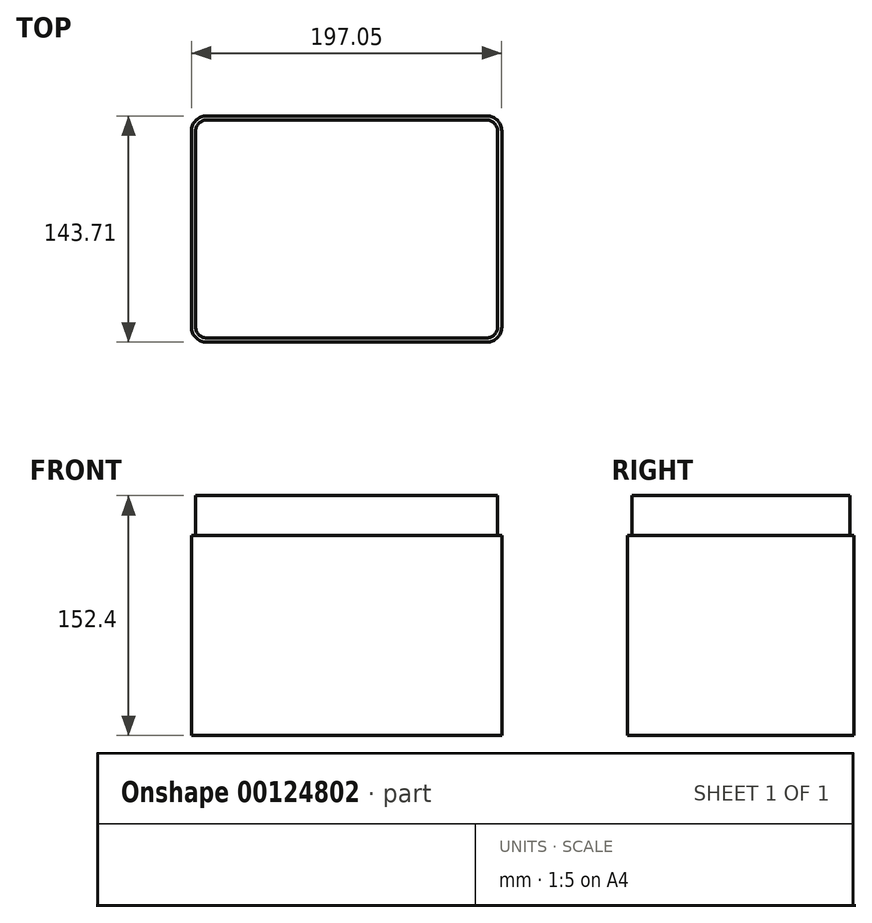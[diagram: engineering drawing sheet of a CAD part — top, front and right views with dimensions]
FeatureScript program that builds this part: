
annotation { "Feature Type Name" : "Feature", "Feature Type Description" : "" }
export const myFeature = defineFeature(function(context is Context, id is Id, definition is map)
    precondition{}
    {
        {
            var Q0;
            Q0=qCreatedBy(makeId("Top.planeOp"),FACE);
            var sketch = newSketch(context, id + "F0", { "sketchPlane" : qUnion([Q0])});
            skLineSegment(sketch, "E0.bottom", {"start": v(-92.39, 67.72) * mm, "end": v(104.66, 67.72) * mm});
            skLineSegment(sketch, "E0.top", {"start": v(-92.39, -76) * mm, "end": v(104.66, -76) * mm});
            skLineSegment(sketch, "E0.left", {"start": v(-92.39, 67.72) * mm, "end": v(-92.39, -76) * mm});
            skLineSegment(sketch, "E0.right", {"start": v(104.66, 67.72) * mm, "end": v(104.66, -76) * mm});
            skSolve(sketch);
        }
        {
            var Q0;
            Q0=makeQuery(id+"F0.imprint","IMPRINT",FACE,{"disambiguationData":[TD([[makeQuery(id+"F0.imprint","IMPRINT",EDGE,{"derivedFrom":sQuery(id+"F0.wireOp",EDGE,"E0.bottom")}),-1.0]])]});
            extrude(context, id + "F1", {"entities" : qUnion([Q0]), "endBound" : BoundingType.SYMMETRIC, "depth" : 152.4 * mm});
        }
        {
            var Q0;
            Q0=makeQuery(id+"F1.opExtrude","SWEPT_EDGE",EDGE,{"disambiguationData":[OSD([sQuery(id+"F0.wireOp",EDGE,"E0.top"),sQuery(id+"F0.wireOp",EDGE,"E0.left")])]});
            var Q1;
            Q1=makeQuery(id+"F1.opExtrude","SWEPT_EDGE",EDGE,{"disambiguationData":[OSD([sQuery(id+"F0.wireOp",EDGE,"E0.bottom"),sQuery(id+"F0.wireOp",EDGE,"E0.left")])]});
            var Q2;
            Q2=makeQuery(id+"F1.opExtrude","SWEPT_EDGE",EDGE,{"disambiguationData":[OSD([sQuery(id+"F0.wireOp",EDGE,"E0.bottom"),sQuery(id+"F0.wireOp",EDGE,"E0.right")])]});
            var Q3;
            Q3=makeQuery(id+"F1.opExtrude","SWEPT_EDGE",EDGE,{"disambiguationData":[OSD([sQuery(id+"F0.wireOp",EDGE,"E0.top"),sQuery(id+"F0.wireOp",EDGE,"E0.right")])]});
            fillet(context, id + "F2", {"entities" : qUnion([Q0, Q1, Q2, Q3]), "radius" : 9.52 * mm, "tangentPropagation" : true, "allowEdgeOverflow" : false});
        }
        {
            var Q0;
            Q0=makeQuery(id+"F1.opExtrude","CAP_FACE",FACE,{"disambiguationData":[OSD([sQuery(id+"F0.wireOp",EDGE,"E0.bottom"),sQuery(id+"F0.wireOp",EDGE,"E0.top"),sQuery(id+"F0.wireOp",EDGE,"E0.left"),sQuery(id+"F0.wireOp",EDGE,"E0.right")])],"isStart":false});
            var sketch = newSketch(context, id + "F3", { "sketchPlane" : qUnion([Q0])});
            skLineSegment(sketch, "E1.0", {"start": v(-82.86, 67.72) * mm, "end": v(95.14, 67.72) * mm});
            skArc(sketch, "E2.0", {"start": v(-82.86, 67.72) * mm, "mid": v(-89.6, 64.93) * mm, "end": v(-92.39, 58.2) * mm});
            skLineSegment(sketch, "E3.0", {"start": v(-92.39, 58.2) * mm, "end": v(-92.39, -66.47) * mm});
            skArc(sketch, "E4.0", {"start": v(-92.39, -66.47) * mm, "mid": v(-89.6, -73.2) * mm, "end": v(-82.86, -76) * mm});
            skLineSegment(sketch, "E5.0", {"start": v(-82.86, -76) * mm, "end": v(95.14, -76) * mm});
            skArc(sketch, "E6.0", {"start": v(95.14, -76) * mm, "mid": v(101.87, -73.2) * mm, "end": v(104.66, -66.47) * mm});
            skLineSegment(sketch, "E7.0", {"start": v(104.66, 58.2) * mm, "end": v(104.66, -66.47) * mm});
            skArc(sketch, "E8.0", {"start": v(104.66, 58.2) * mm, "mid": v(101.87, 64.93) * mm, "end": v(95.14, 67.72) * mm});
            skArc(sketch, "E9.0", {"start": v(-82.86, 65.06) * mm, "mid": v(-87.71, 63.05) * mm, "end": v(-89.72, 58.2) * mm});
            skArc(sketch, "E9.1", {"start": v(95.14, -73.32) * mm, "mid": v(99.99, -71.32) * mm, "end": v(102, -66.47) * mm});
            skLineSegment(sketch, "E9.2", {"start": v(102, 58.2) * mm, "end": v(102, -66.47) * mm});
            skArc(sketch, "E9.3", {"start": v(102, 58.2) * mm, "mid": v(99.99, 63.05) * mm, "end": v(95.14, 65.06) * mm});
            skLineSegment(sketch, "E9.4", {"start": v(-82.86, 65.06) * mm, "end": v(95.14, 65.06) * mm});
            skLineSegment(sketch, "E10.0", {"start": v(-82.86, -73.32) * mm, "end": v(95.14, -73.32) * mm});
            skArc(sketch, "E10.1", {"start": v(-89.72, -66.47) * mm, "mid": v(-87.71, -71.32) * mm, "end": v(-82.86, -73.32) * mm});
            skLineSegment(sketch, "E10.2", {"start": v(-89.72, 58.2) * mm, "end": v(-89.72, -66.47) * mm});
            skSolve(sketch);
        }
        {
            var Q0;
            Q0=makeQuery(id+"F3.imprint","IMPRINT",FACE,{"disambiguationData":[TD([[makeQuery(id+"F3.imprint","IMPRINT",EDGE,{"derivedFrom":sQuery(id+"F3.wireOp",EDGE,"E1.0")}),-1.0]])]});
            extrude(context, id + "F4", {"entities" : qUnion([Q0]), "operationType" : NewBodyOperationType.REMOVE, "oppositeDirection" : true, "depth" : 25.4 * mm});
        }
    });
